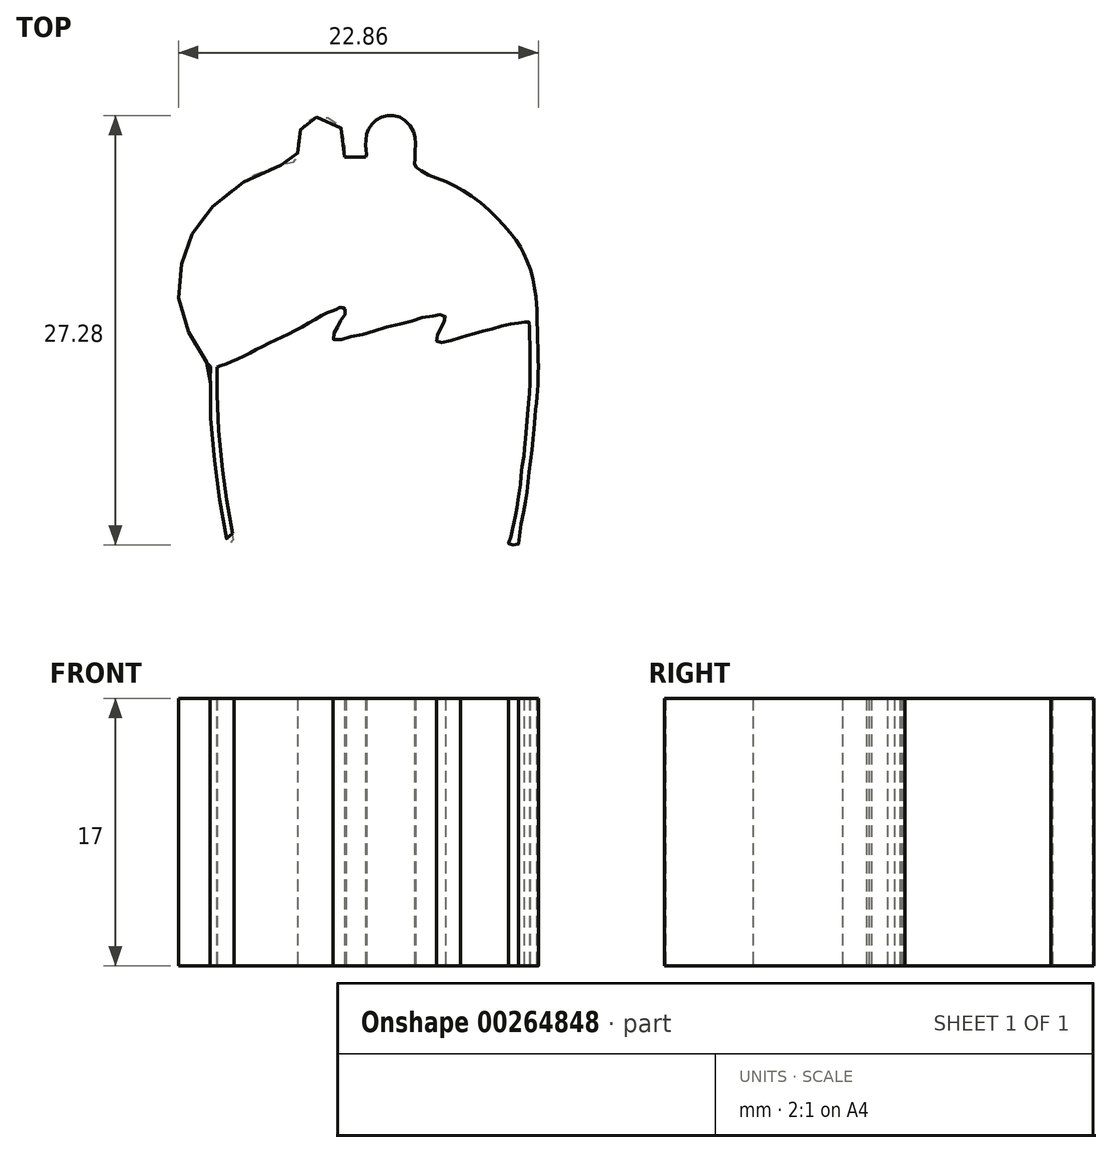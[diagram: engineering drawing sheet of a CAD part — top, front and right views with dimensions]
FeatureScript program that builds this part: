
annotation { "Feature Type Name" : "Feature", "Feature Type Description" : "" }
export const myFeature = defineFeature(function(context is Context, id is Id, definition is map)
    precondition{}
    {
        {
            var Q0;
            Q0=qCreatedBy(makeId("Top.planeOp"),FACE);
            var sketch = newSketch(context, id + "F0", { "sketchPlane" : qUnion([Q0])});
            skFitSpline(sketch, "E0", {"points": [v(-0.7, 15.43) * mm, v(-0.7, 16.03) * mm, v(-0.72, 16.72) * mm, v(-1.07, 17.47) * mm, v(-1.67, 17.86) * mm, v(-2.2, 17.98) * mm, v(-2.67, 17.9) * mm, v(-2.98, 17.75) * mm, v(-3.23, 17.56) * mm, v(-3.44, 17.3) * mm, v(-3.57, 17.04) * mm, v(-3.66, 16.72) * mm, v(-3.7, 16.1) * mm, v(-3.7, 15.6) * mm, v(-3.7, 15.23) * mm, v(-3.77, 15.13) * mm, v(-4.3, 15.04) * mm, v(-5.3, 14.73) * mm, v(-6.65, 14.16) * mm, v(-7.74, 13.39) * mm, v(-8.74, 12.62) * mm, v(-9.45, 11.9) * mm, v(-10, 11.21) * mm, v(-10.48, 10.35) * mm, v(-10.76, 9.64) * mm, v(-11, 8.82) * mm, v(-11.17, 8.13) * mm, v(-11.26, 7.16) * mm, v(-11.22, 6.18) * mm, v(-11, 5.27) * mm, v(-10.61, 4.26) * mm, v(-10.16, 3.32) * mm, v(-9.6, 2.54) * mm, v(-9.3, 2.18) * mm, v(-9.23, 2.13) * mm, v(-9.25, 1.63) * mm, v(-9.24, 1.06) * mm, v(-9.26, 0.37) * mm, v(-9.25, -0.8) * mm, v(-9.2, -1.77) * mm, v(-9.03, -3.31) * mm, v(-8.84, -4.99) * mm, v(-8.72, -5.95) * mm, v(-8.5, -7.17) * mm, v(-8.3, -8.28) * mm, v(-8.13, -9.14) * mm, v(-8.11, -9.14) * mm, v(-7.74, -9.13) * mm, v(-7.72, -9.12) * mm, v(-7.8, -8.63) * mm, v(-7.93, -8) * mm, v(-8.12, -6.78) * mm, v(-8.26, -6) * mm, v(-8.36, -5.25) * mm, v(-8.42, -4.67) * mm, v(-8.55, -3.78) * mm, v(-8.7, -2.35) * mm, v(-8.76, -1.14) * mm, v(-8.81, -0.15) * mm, v(-8.81, 0.82) * mm, v(-8.82, 1.42) * mm, v(-8.82, 2.06) * mm, v(-8.8, 2.1) * mm], "startDerivative": vector(-0.8, 39.25) * mm, "endDerivative": vector(4.46, 6.4) * mm});
            skFitSpline(sketch, "E1", {"points": [v(-8.8, 2.1) * mm, v(-8.4, 2.24) * mm, v(-7.67, 2.52) * mm, v(-6.78, 2.96) * mm, v(-5.81, 3.45) * mm, v(-4.83, 3.93) * mm, v(-3.79, 4.44) * mm, v(-2.68, 5.05) * mm, v(-1.76, 5.56) * mm, v(-1.35, 5.71) * mm, v(-1.03, 5.86) * mm, v(-0.82, 5.85) * mm, v(-0.68, 5.76) * mm], "startDerivative": vector(5.65, 1.9) * mm, "endDerivative": vector(3.17, -2.45) * mm});
            skFitSpline(sketch, "E2", {"points": [v(-0.68, 5.76) * mm, v(-0.61, 5.57) * mm, v(-0.78, 5.3) * mm, v(-0.97, 5) * mm, v(-1.11, 4.72) * mm, v(-1.3, 4.4) * mm, v(-1.42, 4.12) * mm, v(-1.41, 3.83) * mm, v(-1.02, 3.82) * mm, v(-0.43, 3.99) * mm, v(0.48, 4.17) * mm, v(1.43, 4.47) * mm, v(2.69, 4.8) * mm, v(3.65, 5.05) * mm, v(4.39, 5.26) * mm, v(5.07, 5.36) * mm, v(5.34, 5.41) * mm, v(5.58, 5.38) * mm, v(5.7, 5.27) * mm, v(5.62, 5.03) * mm, v(5.5, 4.75) * mm, v(5.3, 4.37) * mm, v(5.18, 4.08) * mm, v(5.12, 3.85) * mm, v(5.18, 3.65) * mm, v(5.42, 3.64) * mm, v(6.02, 3.76) * mm, v(6.65, 3.96) * mm], "startDerivative": vector(4.5, -7.51) * mm, "endDerivative": vector(13.56, 4.53) * mm});
            skFitSpline(sketch, "E3", {"points": [v(6.65, 3.96) * mm, v(7.15, 4.1) * mm, v(7.84, 4.32) * mm, v(8.74, 4.54) * mm, v(9.73, 4.81) * mm, v(10.44, 4.9) * mm, v(10.8, 4.95) * mm, v(11, 4.95) * mm, v(11.03, 4.8) * mm, v(11.04, 4) * mm, v(11.05, 3.1) * mm, v(11.06, 2.1) * mm, v(11.05, 1.1) * mm, v(10.99, 0) * mm, v(10.86, -1.43) * mm, v(10.74, -2.88) * mm, v(10.67, -3.57) * mm], "startDerivative": vector(9.32, 2.38) * mm, "endDerivative": vector(-1.16, -10.46) * mm});
            skFitSpline(sketch, "E4", {"points": [v(10.67, -3.57) * mm, v(10.52, -4.6) * mm, v(10.45, -5.36) * mm, v(10.34, -6.1) * mm, v(10.3, -6.5) * mm, v(10.19, -7.14) * mm, v(10.06, -7.72) * mm, v(9.95, -8.15) * mm, v(9.84, -8.7) * mm, v(9.7, -9.16) * mm, v(9.74, -9.2) * mm, v(10.33, -9.18) * mm, v(10.34, -9.14) * mm, v(10.43, -8.27) * mm, v(10.68, -6.9) * mm, v(10.86, -5.84) * mm, v(10.96, -4.87) * mm, v(11.13, -3.74) * mm, v(11.26, -2.47) * mm], "startDerivative": vector(-2.59, -15.5) * mm, "endDerivative": vector(1.4, 16.63) * mm});
            skFitSpline(sketch, "E5", {"points": [v(11.26, -2.47) * mm, v(11.32, -1.74) * mm, v(11.43, -0.57) * mm, v(11.54, 0.6) * mm, v(11.58, 1.5) * mm, v(11.58, 2.67) * mm, v(11.55, 3.79) * mm, v(11.52, 4.76) * mm, v(11.52, 5.42) * mm, v(11.49, 6.07) * mm], "startDerivative": vector(0.56, 7) * mm, "endDerivative": vector(-0.91, 7.3) * mm});
            skFitSpline(sketch, "E6", {"points": [v(11.49, 6.07) * mm, v(11.41, 6.74) * mm, v(11.26, 7.62) * mm, v(10.96, 8.63) * mm, v(10.63, 9.37) * mm, v(10.37, 9.84) * mm, v(9.84, 10.58) * mm, v(9.17, 11.33) * mm, v(8.18, 12.3) * mm, v(7.1, 13.1) * mm, v(6.27, 13.6) * mm, v(5.2, 14.08) * mm, v(4.42, 14.38) * mm, v(3.93, 14.71) * mm, v(3.83, 14.79) * mm, v(3.73, 14.97) * mm, v(3.75, 15.34) * mm], "startDerivative": vector(-1.2, 10.67) * mm, "endDerivative": vector(-0.34, 9.32) * mm});
            skFitSpline(sketch, "E7", {"points": [v(3.75, 15.34) * mm, v(3.78, 16.03) * mm, v(3.75, 16.66) * mm, v(3.63, 17.11) * mm, v(3.24, 17.64) * mm, v(2.83, 17.94) * mm, v(2.27, 18.07) * mm, v(1.8, 18.01) * mm, v(1.35, 17.8) * mm, v(1, 17.5) * mm, v(0.75, 17.1) * mm, v(0.66, 16.74) * mm, v(0.62, 16.31) * mm, v(0.62, 16.03) * mm, v(0.66, 15.73) * mm, v(0.66, 15.46) * mm, v(0.62, 15.42) * mm, v(0.33, 15.41) * mm, v(-0.19, 15.43) * mm, v(-0.5, 15.43) * mm, v(-0.7, 15.43) * mm], "startDerivative": vector(0.4, 10.64) * mm, "endDerivative": vector(-5.55, -0.03) * mm});
            skCircle(sketch, "E8", {"center": v(6.09, -0.5) * mm, "radius": 3.15 * mm});
            skPoint(sketch, "E8.first.point", {"position": v(5.98, 2.65) * mm});
            skPoint(sketch, "E8.second.point", {"position": v(6.02, -3.65) * mm});
            skPoint(sketch, "E8.third.point", {"position": v(9.22, -0.2) * mm});
            skCircle(sketch, "E9", {"center": v(6.08, -0.54) * mm, "radius": 2.63 * mm});
            skPoint(sketch, "E9.first.point", {"position": v(5.98, 2.1) * mm});
            skPoint(sketch, "E9.second.point", {"position": v(5.98, -3.17) * mm});
            skPoint(sketch, "E9.third.point", {"position": v(8.7, -0.58) * mm});
            skCircle(sketch, "E10", {"center": v(7.16, -0.53) * mm, "radius": 1.28 * mm});
            skPoint(sketch, "E10.first.point", {"position": v(7.12, 0.75) * mm});
            skPoint(sketch, "E10.second.point", {"position": v(7.22, -1.8) * mm});
            skPoint(sketch, "E10.third.point", {"position": v(8.43, -0.49) * mm});
            skCircle(sketch, "E11", {"center": v(-4.02, -0.63) * mm, "radius": 3.11 * mm});
            skPoint(sketch, "E11.first.point", {"position": v(-4.2, 2.47) * mm});
            skPoint(sketch, "E11.second.point", {"position": v(-3.86, -3.74) * mm});
            skPoint(sketch, "E11.third.point", {"position": v(-1.05, 0.3) * mm});
            skCircle(sketch, "E12", {"center": v(-4.04, -0.66) * mm, "radius": 2.65 * mm});
            skPoint(sketch, "E12.first.point", {"position": v(-4.2, 1.99) * mm});
            skPoint(sketch, "E12.second.point", {"position": v(-3.9, -3.3) * mm});
            skPoint(sketch, "E12.third.point", {"position": v(-1.39, -0.71) * mm});
            skCircle(sketch, "E13", {"center": v(-2.97, -0.61) * mm, "radius": 1.26 * mm});
            skPoint(sketch, "E13.first.point", {"position": v(-2.97, 0.64) * mm});
            skPoint(sketch, "E13.second.point", {"position": v(-2.96, -1.87) * mm});
            skPoint(sketch, "E13.third.point", {"position": v(-1.72, -0.58) * mm});
            skFitSpline(sketch, "E14", {"points": [v(0.31, -3.75) * mm, v(0.56, -3.78) * mm, v(0.87, -3.93) * mm, v(0.95, -3.99) * mm, v(1.05, -3.93) * mm, v(1.33, -3.75) * mm, v(1.71, -3.7) * mm, v(2, -3.87) * mm, v(2.13, -4.19) * mm, v(2.02, -4.46) * mm, v(1.77, -4.62) * mm, v(1.4, -4.73) * mm, v(1, -4.78) * mm, v(0.6, -4.75) * mm, v(0.25, -4.68) * mm, v(0, -4.54) * mm, v(-0.17, -4.24) * mm, v(-0.13, -3.95) * mm, v(0.05, -3.79) * mm, v(0.31, -3.75) * mm]});
            skSolve(sketch);
        }
        {
            var Q0;
            Q0=makeQuery(id+"F0.imprint","IMPRINT",FACE,{"disambiguationData":[TD([[makeQuery(id+"F0.imprint","IMPRINT",EDGE,{"derivedFrom":sQuery(id+"F0.wireOp",EDGE,"E0")}),1.0]])]});
            extrude(context, id + "F1", {"entities" : qUnion([Q0]), "depth" : 17 * mm});
        }
    });
